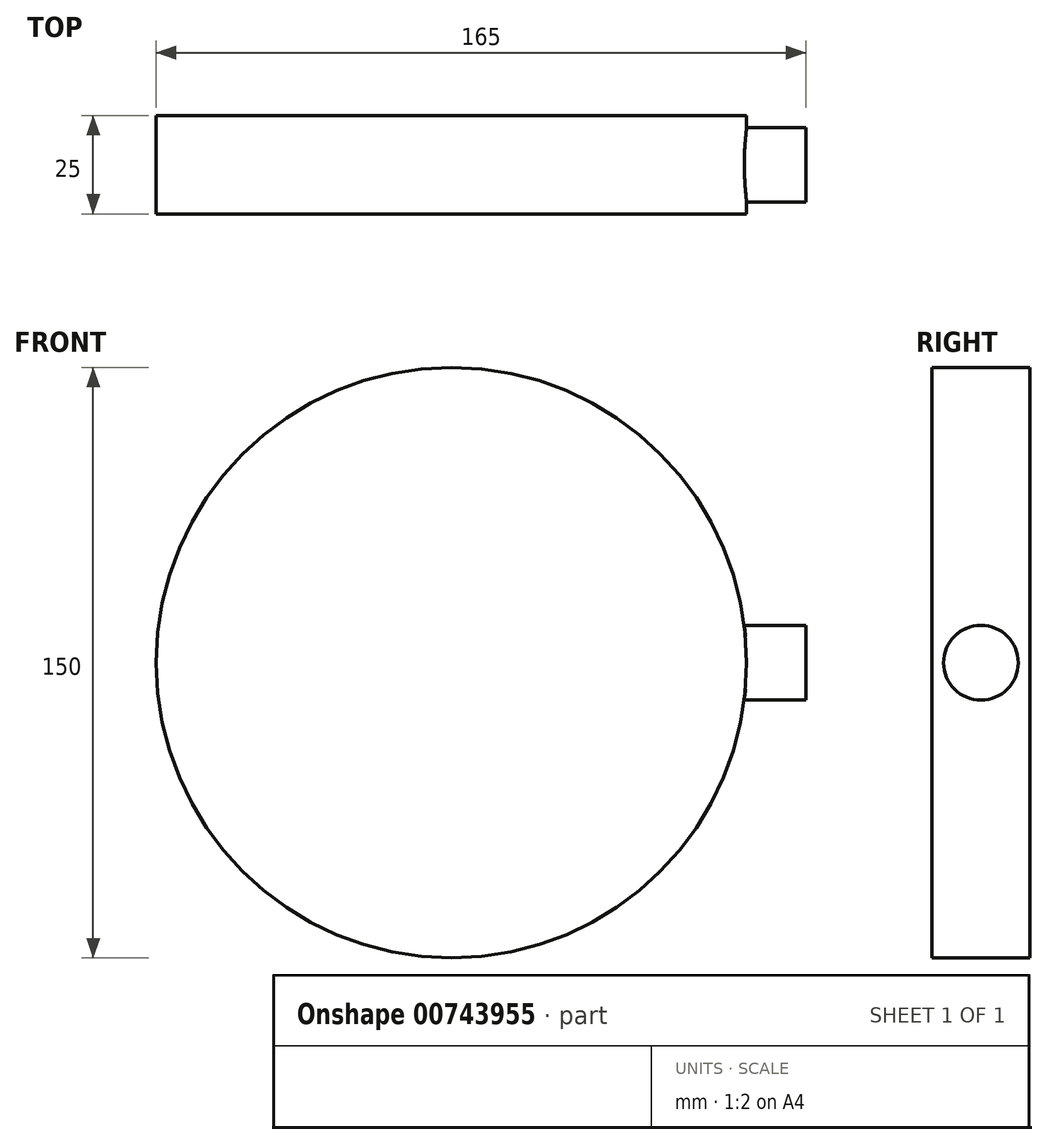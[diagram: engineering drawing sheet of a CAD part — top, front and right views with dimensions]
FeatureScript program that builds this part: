
annotation { "Feature Type Name" : "Feature", "Feature Type Description" : "" }
export const myFeature = defineFeature(function(context is Context, id is Id, definition is map)
    precondition{}
    {
        {
            var Q0;
            Q0=qCreatedBy(makeId("Front.planeOp"),FACE);
            var sketch = newSketch(context, id + "F0", { "sketchPlane" : qUnion([Q0])});
            skCircle(sketch, "E0", {"center": v(0, 0) * mm, "radius": 75 * mm});
            skSolve(sketch);
        }
        {
            var Q0;
            Q0=makeQuery(id+"F0.imprint","IMPRINT",FACE,{"disambiguationData":[TD([[makeQuery(id+"F0.imprint","IMPRINT",EDGE,{"derivedFrom":sQuery(id+"F0.wireOp",EDGE,"E0")}),1.0]])]});
            extrude(context, id + "F1", {"entities" : qUnion([Q0]), "endBound" : BoundingType.SYMMETRIC, "oppositeDirection" : true, "depth" : 25 * mm, "offsetDistance" : 25 * mm});
        }
        {
            var Q0;
            Q0=qCreatedBy(makeId("Right.planeOp"),FACE);
            cPlane(context, id + "F2", {"entities" : qUnion([Q0]), "cplaneType" : CPlaneType.OFFSET, "offset" : 65 * mm, "width" : 150 * mm, "height" : 150 * mm});
        }
        {
            var Q0;
            Q0=qCreatedBy(id+"F2.planeOp",FACE);
            var sketch = newSketch(context, id + "F3", { "sketchPlane" : qUnion([Q0])});
            skCircle(sketch, "E1", {"center": v(0, 0) * mm, "radius": 9.5 * mm});
            skSolve(sketch);
        }
        {
            var Q0;
            Q0 = qSketchRegion(id + "F3", true);
            extrude(context, id + "F4", {"entities" : qUnion([Q0]), "operationType" : NewBodyOperationType.ADD, "depth" : 25 * mm, "offsetDistance" : 25 * mm});
        }
    });
